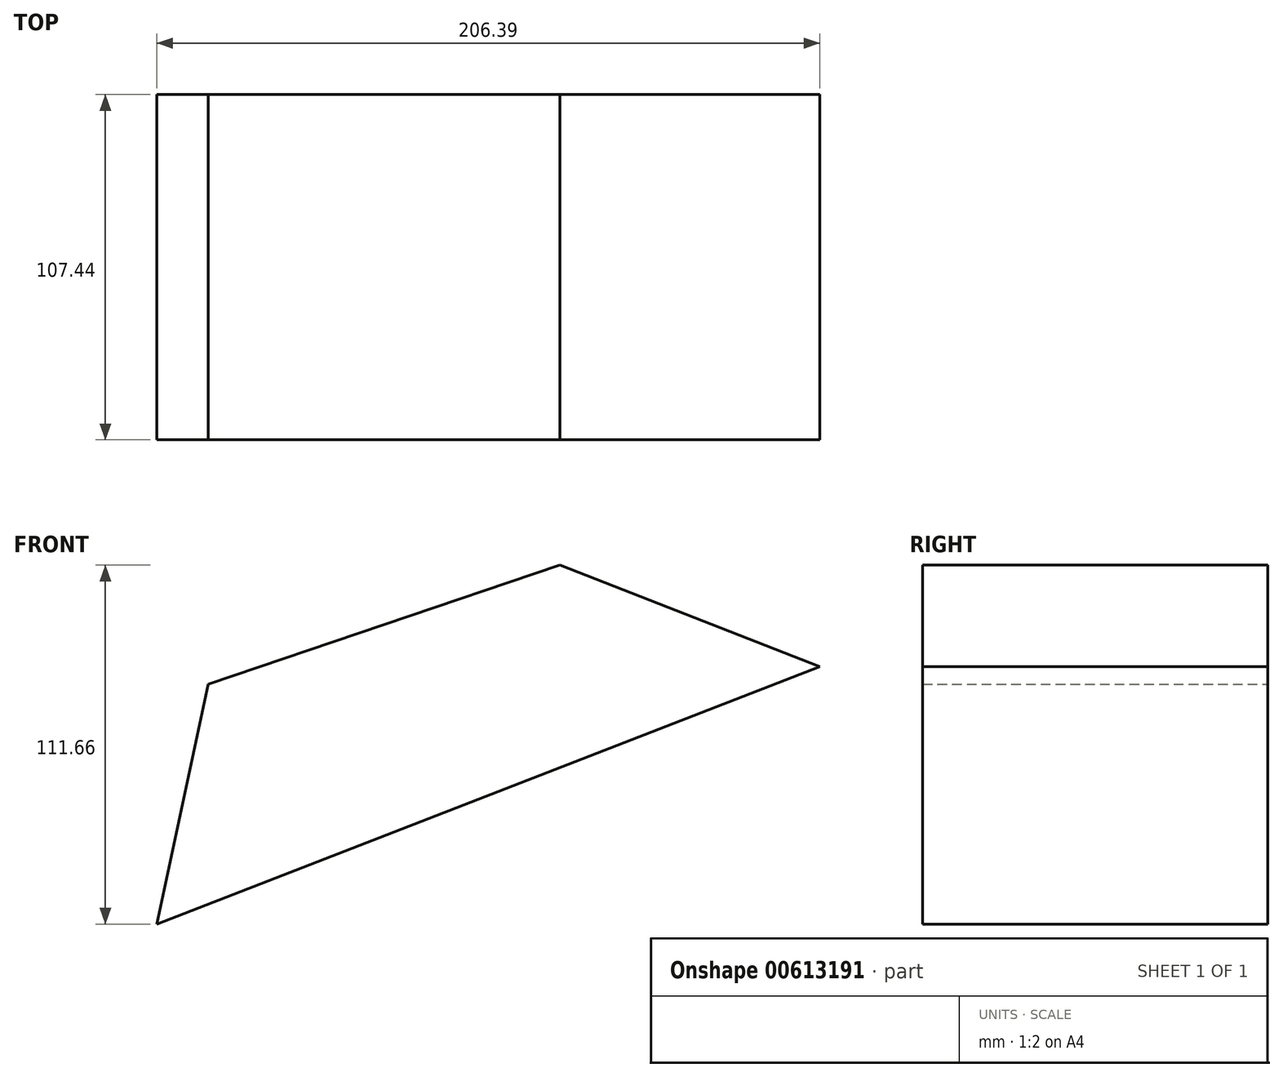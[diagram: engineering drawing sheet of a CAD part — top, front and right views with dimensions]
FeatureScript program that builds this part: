
annotation { "Feature Type Name" : "Feature", "Feature Type Description" : "" }
export const myFeature = defineFeature(function(context is Context, id is Id, definition is map)
    precondition{}
    {
        {
            var Q0;
            Q0=qCreatedBy(makeId("Front.planeOp"),FACE);
            var sketch = newSketch(context, id + "F0", { "sketchPlane" : qUnion([Q0])});
            skLineSegment(sketch, "E0", {"start": v(-100.56, 70.78) * mm, "end": v(-116.55, -3.8) * mm});
            skLineSegment(sketch, "E1", {"start": v(-116.55, -3.8) * mm, "end": v(89.84, 76.27) * mm});
            skLineSegment(sketch, "E2", {"start": v(89.84, 76.27) * mm, "end": v(8.88, 107.87) * mm});
            skLineSegment(sketch, "E3", {"start": v(8.88, 107.87) * mm, "end": v(-100.56, 70.78) * mm});
            skSolve(sketch);
        }
        {
            var Q0;
            Q0=makeQuery(id+"F0.imprint","IMPRINT",FACE,{"disambiguationData":[TD([[makeQuery(id+"F0.imprint","IMPRINT",EDGE,{"derivedFrom":sQuery(id+"F0.wireOp",EDGE,"E0")}),1.0]])]});
            extrude(context, id + "F1", {"entities" : qUnion([Q0]), "depth" : 107.44 * mm, "offsetDistance" : 25.4 * mm});
        }
    });
